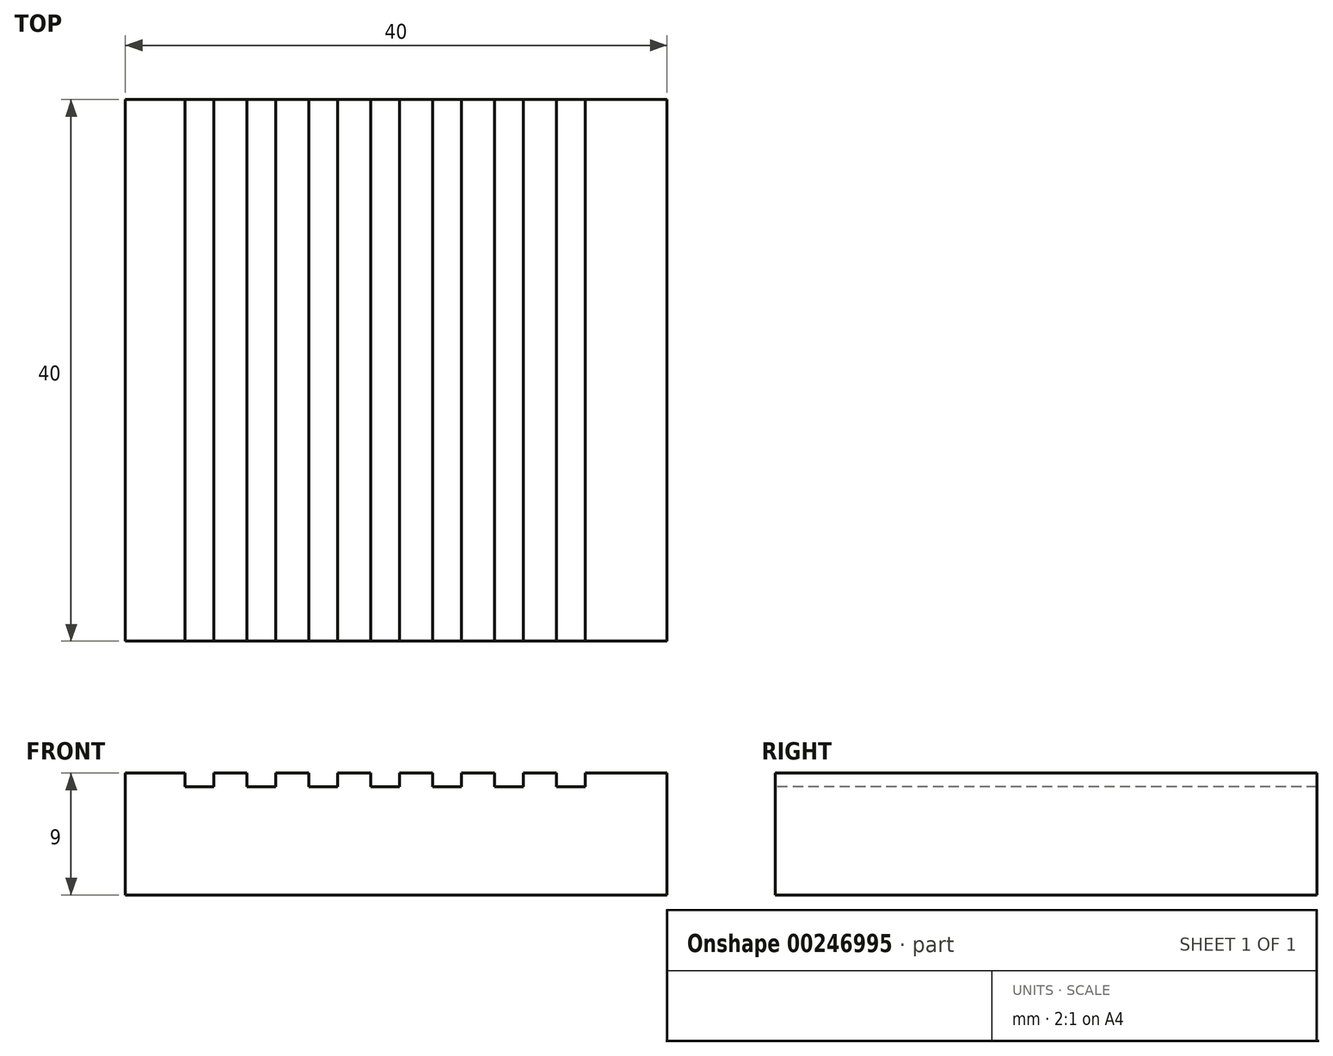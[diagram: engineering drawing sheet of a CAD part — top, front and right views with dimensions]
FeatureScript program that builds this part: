
annotation { "Feature Type Name" : "Feature", "Feature Type Description" : "" }
export const myFeature = defineFeature(function(context is Context, id is Id, definition is map)
    precondition{}
    {
        {
            var Q0;
            Q0=qCreatedBy(makeId("Front.planeOp"),FACE);
            var sketch = newSketch(context, id + "F0", { "sketchPlane" : qUnion([Q0])});
            skLineSegment(sketch, "E0.bottom", {"start": v(0, 0) * mm, "end": v(40, 0) * mm});
            skLineSegment(sketch, "E0.top", {"start": v(0, 9) * mm, "end": v(40, 9) * mm});
            skLineSegment(sketch, "E0.left", {"start": v(0, 0) * mm, "end": v(0, 9) * mm});
            skLineSegment(sketch, "E0.right", {"start": v(40, 0) * mm, "end": v(40, 9) * mm});
            skSolve(sketch);
        }
        {
            var Q0;
            Q0=makeQuery(id+"F0.imprint","IMPRINT",FACE,{"disambiguationData":[TD([[makeQuery(id+"F0.imprint","IMPRINT",EDGE,{"derivedFrom":sQuery(id+"F0.wireOp",EDGE,"E0.bottom")}),1.0]])]});
            extrude(context, id + "F1", {"entities" : qUnion([Q0]), "depth" : 40 * mm});
        }
        {
            var Q0;
            Q0=makeQuery(id+"F1.opExtrude","CAP_FACE",FACE,{"disambiguationData":[OSD([sQuery(id+"F0.wireOp",EDGE,"E0.bottom"),sQuery(id+"F0.wireOp",EDGE,"E0.top"),sQuery(id+"F0.wireOp",EDGE,"E0.left"),sQuery(id+"F0.wireOp",EDGE,"E0.right")])],"isStart":false});
            var sketch = newSketch(context, id + "F2", { "sketchPlane" : qUnion([Q0])});
            skLineSegment(sketch, "E1.bottom", {"start": v(4.42, 9) * mm, "end": v(6.52, 9) * mm});
            skLineSegment(sketch, "E1.top", {"start": v(4.42, 7.98) * mm, "end": v(6.52, 7.98) * mm});
            skLineSegment(sketch, "E1.left", {"start": v(4.42, 9) * mm, "end": v(4.42, 7.98) * mm});
            skLineSegment(sketch, "E1.right", {"start": v(6.52, 9) * mm, "end": v(6.52, 7.98) * mm});
            skLineSegment(sketch, "E2.1.0.0", {"start": v(8.99, 9) * mm, "end": v(11.1, 9) * mm});
            skLineSegment(sketch, "E2.1.0.1", {"start": v(8.99, 7.98) * mm, "end": v(11.1, 7.98) * mm});
            skLineSegment(sketch, "E2.1.0.2", {"start": v(8.99, 9) * mm, "end": v(8.99, 7.98) * mm});
            skLineSegment(sketch, "E2.1.0.3", {"start": v(11.1, 9) * mm, "end": v(11.1, 7.98) * mm});
            skLineSegment(sketch, "E2.2.0.0", {"start": v(13.56, 9) * mm, "end": v(15.66, 9) * mm});
            skLineSegment(sketch, "E2.2.0.1", {"start": v(13.56, 7.98) * mm, "end": v(15.66, 7.98) * mm});
            skLineSegment(sketch, "E2.2.0.2", {"start": v(13.56, 9) * mm, "end": v(13.56, 7.98) * mm});
            skLineSegment(sketch, "E2.2.0.3", {"start": v(15.66, 9) * mm, "end": v(15.66, 7.98) * mm});
            skLineSegment(sketch, "E2.3.0.0", {"start": v(18.13, 9) * mm, "end": v(20.24, 9) * mm});
            skLineSegment(sketch, "E2.3.0.1", {"start": v(18.13, 7.98) * mm, "end": v(20.24, 7.98) * mm});
            skLineSegment(sketch, "E2.3.0.2", {"start": v(18.13, 9) * mm, "end": v(18.13, 7.98) * mm});
            skLineSegment(sketch, "E2.3.0.3", {"start": v(20.24, 9) * mm, "end": v(20.24, 7.98) * mm});
            skLineSegment(sketch, "E2.4.0.0", {"start": v(22.7, 9) * mm, "end": v(24.8, 9) * mm});
            skLineSegment(sketch, "E2.4.0.1", {"start": v(22.7, 7.98) * mm, "end": v(24.8, 7.98) * mm});
            skLineSegment(sketch, "E2.4.0.2", {"start": v(22.7, 9) * mm, "end": v(22.7, 7.98) * mm});
            skLineSegment(sketch, "E2.4.0.3", {"start": v(24.8, 9) * mm, "end": v(24.8, 7.98) * mm});
            skLineSegment(sketch, "E2.5.0.0", {"start": v(27.28, 9) * mm, "end": v(29.38, 9) * mm});
            skLineSegment(sketch, "E2.5.0.1", {"start": v(27.28, 7.98) * mm, "end": v(29.38, 7.98) * mm});
            skLineSegment(sketch, "E2.5.0.2", {"start": v(27.28, 9) * mm, "end": v(27.28, 7.98) * mm});
            skLineSegment(sketch, "E2.5.0.3", {"start": v(29.38, 9) * mm, "end": v(29.38, 7.98) * mm});
            skLineSegment(sketch, "E2.6.0.0", {"start": v(31.85, 9) * mm, "end": v(33.95, 9) * mm});
            skLineSegment(sketch, "E2.6.0.1", {"start": v(31.85, 7.98) * mm, "end": v(33.95, 7.98) * mm});
            skLineSegment(sketch, "E2.6.0.2", {"start": v(31.85, 9) * mm, "end": v(31.85, 7.98) * mm});
            skLineSegment(sketch, "E2.6.0.3", {"start": v(33.95, 9) * mm, "end": v(33.95, 7.98) * mm});
            skLineSegment(sketch, "E2.direction1", {"start": v(4.42, 7.98) * mm, "end": v(8.99, 7.98) * mm, "construction": true});
            skSolve(sketch);
        }
        {
            var Q0;
            Q0=makeQuery(id+"F2.imprint","IMPRINT",FACE,{"disambiguationData":[TD([[makeQuery(id+"F2.imprint","IMPRINT",EDGE,{"derivedFrom":sQuery(id+"F2.wireOp",EDGE,"E1.bottom")}),-1.0]])]});
            var Q1;
            Q1=makeQuery(id+"F2.imprint","IMPRINT",FACE,{"disambiguationData":[TD([[makeQuery(id+"F2.imprint","IMPRINT",EDGE,{"derivedFrom":sQuery(id+"F2.wireOp",EDGE,"E2.1.0.0")}),-1.0]])]});
            var Q2;
            Q2=makeQuery(id+"F2.imprint","IMPRINT",FACE,{"disambiguationData":[TD([[makeQuery(id+"F2.imprint","IMPRINT",EDGE,{"derivedFrom":sQuery(id+"F2.wireOp",EDGE,"E2.2.0.0")}),-1.0]])]});
            var Q3;
            Q3=makeQuery(id+"F2.imprint","IMPRINT",FACE,{"disambiguationData":[TD([[makeQuery(id+"F2.imprint","IMPRINT",EDGE,{"derivedFrom":sQuery(id+"F2.wireOp",EDGE,"E2.3.0.0")}),-1.0]])]});
            var Q4;
            Q4=makeQuery(id+"F2.imprint","IMPRINT",FACE,{"disambiguationData":[TD([[makeQuery(id+"F2.imprint","IMPRINT",EDGE,{"derivedFrom":sQuery(id+"F2.wireOp",EDGE,"E2.4.0.0")}),-1.0]])]});
            var Q5;
            Q5=makeQuery(id+"F2.imprint","IMPRINT",FACE,{"disambiguationData":[TD([[makeQuery(id+"F2.imprint","IMPRINT",EDGE,{"derivedFrom":sQuery(id+"F2.wireOp",EDGE,"E2.5.0.0")}),-1.0]])]});
            var Q6;
            Q6=makeQuery(id+"F2.imprint","IMPRINT",FACE,{"disambiguationData":[TD([[makeQuery(id+"F2.imprint","IMPRINT",EDGE,{"derivedFrom":sQuery(id+"F2.wireOp",EDGE,"E2.6.0.0")}),-1.0]])]});
            extrude(context, id + "F3", {"entities" : qUnion([Q0, Q1, Q2, Q3, Q4, Q5, Q6]), "operationType" : NewBodyOperationType.REMOVE, "endBound" : BoundingType.THROUGH_ALL, "oppositeDirection" : true, "depth" : 25.4 * mm});
        }
    });
